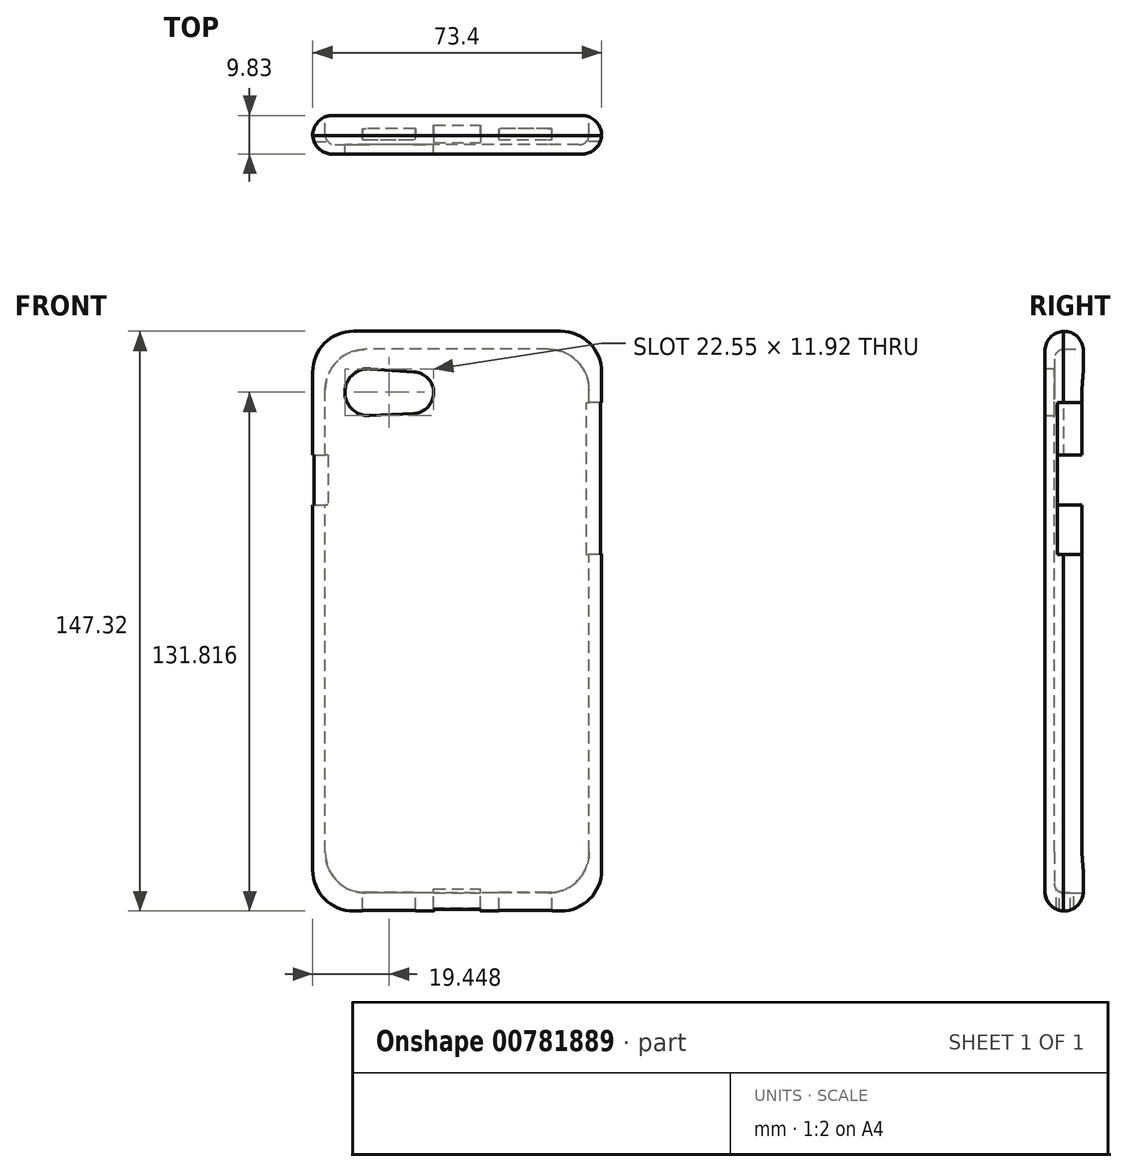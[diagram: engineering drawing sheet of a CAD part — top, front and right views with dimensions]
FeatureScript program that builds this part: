
annotation { "Feature Type Name" : "Feature", "Feature Type Description" : "" }
export const myFeature = defineFeature(function(context is Context, id is Id, definition is map)
    precondition{}
    {
        {
            var Q0;
            Q0=qCreatedBy(makeId("Front.planeOp"),FACE);
            var sketch = newSketch(context, id + "F0", { "sketchPlane" : qUnion([Q0])});
            skLineSegment(sketch, "E0.bottom", {"start": v(36.7, -73.66) * mm, "end": v(-36.7, -73.66) * mm});
            skLineSegment(sketch, "E0.top", {"start": v(36.7, 73.66) * mm, "end": v(-36.7, 73.66) * mm});
            skLineSegment(sketch, "E0.left", {"start": v(36.7, -73.66) * mm, "end": v(36.7, 73.66) * mm});
            skLineSegment(sketch, "E0.right", {"start": v(-36.7, -73.66) * mm, "end": v(-36.7, 73.66) * mm});
            skPoint(sketch, "E0.middle", {"position": v(0, 0) * mm});
            skCircle(sketch, "E1", {"center": v(-22.56, 58.16) * mm, "radius": 5.97 * mm});
            skLineSegment(sketch, "E2", {"start": v(-26.85, 73.66) * mm, "end": v(-26.85, 71.54) * mm});
            skLineSegment(sketch, "E3", {"start": v(-36.7, 59.19) * mm, "end": v(-34.57, 59.19) * mm});
            skLineSegment(sketch, "E4", {"start": v(-36.7, 73.66) * mm, "end": v(-28.82, 65.04) * mm});
            skCircle(sketch, "E5", {"center": v(-11.28, 58.05) * mm, "radius": 5.3 * mm});
            skLineSegment(sketch, "E6", {"start": v(-11.03, 52.74) * mm, "end": v(-22.27, 52.2) * mm});
            skLineSegment(sketch, "E7", {"start": v(-10.92, 63.34) * mm, "end": v(-22.15, 64.11) * mm});
            skLineSegment(sketch, "E8", {"start": v(-28.82, 65.04) * mm, "end": v(-22.15, 57.75) * mm});
            skLineSegment(sketch, "E9", {"start": v(-34.72, 71.5) * mm, "end": v(-36.7, 73.66) * mm});
            skLineSegment(sketch, "E10", {"start": v(-36.7, 73.66) * mm, "end": v(-33.75, 70.43) * mm});
            skSolve(sketch);
        }
        {
            var Q0;
            Q0 = qSketchRegion(id + "F0", true);
            extrude(context, id + "F1", {"entities" : qUnion([Q0]), "depth" : 9.83 * mm, "offsetDistance" : 25.4 * mm});
        }
        {
            var Q0;
            Q0=makeQuery(id+"F1.opExtrude","SWEPT_EDGE",EDGE,{"disambiguationData":[OSD([sQuery(id+"F0.wireOp",EDGE,"E0.bottom"),sQuery(id+"F0.wireOp",EDGE,"E0.left")])]});
            var Q1;
            Q1=makeQuery(id+"F1.opExtrude","SWEPT_EDGE",EDGE,{"disambiguationData":[OSD([sQuery(id+"F0.wireOp",EDGE,"E0.top"),sQuery(id+"F0.wireOp",EDGE,"E0.left")])]});
            var Q2;
            Q2=makeQuery(id+"F1.opExtrude","SWEPT_EDGE",EDGE,{"disambiguationData":[OSD([sQuery(id+"F0.wireOp",EDGE,"E0.bottom"),sQuery(id+"F0.wireOp",EDGE,"E0.right")])]});
            var Q3;
            Q3=makeQuery(id+"F1.opExtrude","SWEPT_EDGE",EDGE,{"disambiguationData":[OSD([sQuery(id+"F0.wireOp",EDGE,"E0.top"),sQuery(id+"F0.wireOp",EDGE,"E0.right")])]});
            fillet(context, id + "F2", {"entities" : qUnion([Q0, Q1, Q2, Q3]), "radius" : 10.4 * mm, "tangentPropagation" : true, "allowEdgeOverflow" : false});
        }
        {
            var Q0;
            Q0=qCreatedBy(makeId("Front.planeOp"),FACE);
            var sketch = newSketch(context, id + "F3", { "sketchPlane" : qUnion([Q0])});
            skLineSegment(sketch, "E11.bottom", {"start": v(33.53, -69.09) * mm, "end": v(-33.53, -69.09) * mm});
            skLineSegment(sketch, "E11.top", {"start": v(33.53, 69.09) * mm, "end": v(-33.53, 69.09) * mm});
            skLineSegment(sketch, "E11.left", {"start": v(33.53, -69.09) * mm, "end": v(33.53, 69.09) * mm});
            skLineSegment(sketch, "E11.right", {"start": v(-33.53, -69.09) * mm, "end": v(-33.53, 69.09) * mm});
            skPoint(sketch, "E11.middle", {"position": v(0, 0) * mm});
            skLineSegment(sketch, "E12", {"start": v(-33.53, -30.02) * mm, "end": v(-37.19, -30.02) * mm});
            skLineSegment(sketch, "E13", {"start": v(-6.36, 69.09) * mm, "end": v(-6.36, 72.75) * mm});
            skSolve(sketch);
        }
        {
            var Q0;
            {var subQ5=sQuery(id+"F3.wireOp",EDGE,"E11.bottom");Q0=makeQuery(id+"F3.imprint","IMPRINT",FACE,{"disambiguationData":[TD([[makeQuery(id+"F3.imprint","IMPRINT",EDGE,{"derivedFrom":subQ5}),-1.0]])]});}
            extrude(context, id + "F4", {"entities" : qUnion([Q0]), "operationType" : NewBodyOperationType.REMOVE, "depth" : 7.44 * mm, "offsetDistance" : 25.4 * mm});
        }
        {
            var Q0;
            Q0=qCreatedBy(makeId("Front.planeOp"),FACE);
            var sketch = newSketch(context, id + "F5", { "sketchPlane" : qUnion([Q0])});
            skLineSegment(sketch, "E14.bottom", {"start": v(31.5, -66.88) * mm, "end": v(-31.5, -66.88) * mm});
            skLineSegment(sketch, "E14.top", {"start": v(31.5, 66.88) * mm, "end": v(-31.5, 66.88) * mm});
            skLineSegment(sketch, "E14.left", {"start": v(31.5, -66.88) * mm, "end": v(31.5, 66.88) * mm});
            skLineSegment(sketch, "E14.right", {"start": v(-31.5, -66.88) * mm, "end": v(-31.5, 66.88) * mm});
            skPoint(sketch, "E14.middle", {"position": v(0, 0) * mm});
            skLineSegment(sketch, "E15", {"start": v(31.5, 66.88) * mm, "end": v(29.58, 65) * mm});
            skCircle(sketch, "E16", {"center": v(23.33, 58.66) * mm, "radius": 5.97 * mm});
            skLineSegment(sketch, "E17", {"start": v(23.37, 66.8) * mm, "end": v(23.37, 64.66) * mm});
            skLineSegment(sketch, "E18", {"start": v(31.4, 58.55) * mm, "end": v(29.26, 58.55) * mm});
            skLineSegment(sketch, "E19", {"start": v(29.58, 65) * mm, "end": v(27.59, 63.07) * mm});
            skLineSegment(sketch, "E20", {"start": v(29.26, 58.66) * mm, "end": v(6.77, 58.66) * mm});
            skCircle(sketch, "E21", {"center": v(12.08, 58.66) * mm, "radius": 5.28 * mm});
            skLineSegment(sketch, "E22", {"start": v(11.76, 63.92) * mm, "end": v(22.96, 64.62) * mm});
            skLineSegment(sketch, "E23", {"start": v(22.96, 52.7) * mm, "end": v(11.76, 53.4) * mm});
            skSolve(sketch);
        }
        {
            var Q0;
            Q0=makeQuery(id+"F4.boolean.opBoolean","COPY",EDGE,{"derivedFrom":makeQuery(id+"F4.opExtrude","SWEPT_EDGE",EDGE,{"disambiguationData":[OSD([sQuery(id+"F3.wireOp",EDGE,"E11.top"),sQuery(id+"F3.wireOp",EDGE,"E11.right")])]})});
            var Q1;
            Q1=makeQuery(id+"F4.boolean.opBoolean","COPY",EDGE,{"derivedFrom":makeQuery(id+"F4.opExtrude","SWEPT_EDGE",EDGE,{"disambiguationData":[OSD([sQuery(id+"F3.wireOp",EDGE,"E11.top"),sQuery(id+"F3.wireOp",EDGE,"E11.left")])]})});
            var Q2;
            Q2=makeQuery(id+"F4.boolean.opBoolean","COPY",EDGE,{"derivedFrom":makeQuery(id+"F4.opExtrude","SWEPT_EDGE",EDGE,{"disambiguationData":[OSD([sQuery(id+"F3.wireOp",EDGE,"E11.bottom"),sQuery(id+"F3.wireOp",EDGE,"E11.left")])]})});
            var Q3;
            Q3=makeQuery(id+"F4.boolean.opBoolean","COPY",EDGE,{"derivedFrom":makeQuery(id+"F4.opExtrude","SWEPT_EDGE",EDGE,{"disambiguationData":[OSD([sQuery(id+"F3.wireOp",EDGE,"E11.bottom"),sQuery(id+"F3.wireOp",EDGE,"E11.right")])]})});
            fillet(context, id + "F6", {"entities" : qUnion([Q0, Q1, Q2, Q3]), "radius" : 10.4 * mm, "tangentPropagation" : true, "allowEdgeOverflow" : false});
        }
        {
            var Q0;
            {var subQ0=sQuery(id+"F5.wireOp",EDGE,"E16");var subQ2=makeQuery(id+"F5.imprint","IMPRINT",VERTEX,{"derivedFrom":subQ0});Q0=makeQuery(id+"F5.imprint","IMPRINT",FACE,{"disambiguationData":[TD([[makeQuery(id+"F5.imprint","IMPRINT",EDGE,{"disambiguationData":[TD([[subQ2,1.0]])],"derivedFrom":subQ0}),1.0]])]});}
            var Q1;
            {var subQ0=sQuery(id+"F5.wireOp",EDGE,"E21");var subQ1=sQuery(id+"F5.wireOp",EDGE,"E16");var subQ2=makeQuery(id+"F5.imprint","INTERSECT",VERTEX,{"disambiguationData":[OD(0.0)],"derivedFrom":[subQ1,subQ0]});Q1=makeQuery(id+"F5.imprint","IMPRINT",FACE,{"disambiguationData":[TD([[makeQuery(id+"F5.imprint","IMPRINT",EDGE,{"disambiguationData":[TD([[subQ2,-1.0]])],"derivedFrom":subQ1}),-1.0]])]});}
            var Q2;
            {var subQ0=sQuery(id+"F5.wireOp",EDGE,"E20");var subQ1=sQuery(id+"F5.wireOp",EDGE,"E16");var subQ2=makeQuery(id+"F5.imprint","INTERSECT",VERTEX,{"derivedFrom":[subQ1,subQ0]});Q2=makeQuery(id+"F5.imprint","IMPRINT",FACE,{"disambiguationData":[TD([[makeQuery(id+"F5.imprint","IMPRINT",EDGE,{"disambiguationData":[TD([[subQ2,-1.0]])],"derivedFrom":subQ1}),-1.0]])]});}
            var Q3;
            {var subQ0=sQuery(id+"F5.wireOp",EDGE,"E23");Q3=makeQuery(id+"F5.imprint","IMPRINT",FACE,{"disambiguationData":[TD([[makeQuery(id+"F5.imprint","IMPRINT",EDGE,{"derivedFrom":subQ0}),-1.0]])]});}
            var Q4;
            {var subQ0=sQuery(id+"F5.wireOp",EDGE,"E22");Q4=makeQuery(id+"F5.imprint","IMPRINT",FACE,{"disambiguationData":[TD([[makeQuery(id+"F5.imprint","IMPRINT",EDGE,{"derivedFrom":subQ0}),-1.0]])]});}
            extrude(context, id + "F7", {"entities" : qUnion([Q0, Q1, Q2, Q3, Q4]), "operationType" : NewBodyOperationType.REMOVE, "oppositeDirection" : true, "depth" : 25.4 * mm, "offsetDistance" : 25.4 * mm});
        }
        {
            var Q0;
            Q0=makeQuery(id+"F1.opExtrude","CAP_EDGE",EDGE,{"disambiguationData":[OSD([sQuery(id+"F0.wireOp",EDGE,"E0.right")])],"isStart":true});
            fillet(context, id + "F8", {"entities" : qUnion([Q0]), "radius" : 5.08 * mm, "tangentPropagation" : true, "allowEdgeOverflow" : false});
        }
        {
            var Q0;
            Q0=makeQuery(id+"F1.opExtrude","CAP_EDGE",EDGE,{"disambiguationData":[OSD([sQuery(id+"F0.wireOp",EDGE,"E0.right")])],"isStart":false});
            fillet(context, id + "F9", {"entities" : qUnion([Q0]), "radius" : 5.08 * mm, "tangentPropagation" : true, "allowEdgeOverflow" : false});
        }
        {
            var Q0;
            Q0=qCreatedBy(makeId("Top.planeOp"),FACE);
            var sketch = newSketch(context, id + "F10", { "sketchPlane" : qUnion([Q0])});
            skLineSegment(sketch, "E24.bottom", {"start": v(5.97, -2.5) * mm, "end": v(-5.97, -2.5) * mm});
            skLineSegment(sketch, "E24.top", {"start": v(5.97, -6.94) * mm, "end": v(-5.97, -6.94) * mm});
            skLineSegment(sketch, "E24.left", {"start": v(5.97, -2.5) * mm, "end": v(5.97, -6.94) * mm});
            skLineSegment(sketch, "E24.right", {"start": v(-5.97, -2.5) * mm, "end": v(-5.97, -6.94) * mm});
            skPoint(sketch, "E24.middle", {"position": v(0, -4.72) * mm});
            skLineSegment(sketch, "E25", {"start": v(5.97, -5.08) * mm, "end": v(10.57, -5.08) * mm});
            skLineSegment(sketch, "E26", {"start": v(-10.57, -5.08) * mm, "end": v(-5.97, -5.08) * mm});
            skLineSegment(sketch, "E27.bottom", {"start": v(-24.06, -6.13) * mm, "end": v(-10.58, -6.13) * mm});
            skLineSegment(sketch, "E27.top", {"start": v(-24.06, -3.31) * mm, "end": v(-10.58, -3.31) * mm});
            skLineSegment(sketch, "E27.left", {"start": v(-24.06, -6.13) * mm, "end": v(-24.06, -3.31) * mm});
            skLineSegment(sketch, "E27.right", {"start": v(-10.58, -6.13) * mm, "end": v(-10.58, -3.31) * mm});
            skPoint(sketch, "E27.middle", {"position": v(-17.32, -4.72) * mm});
            skLineSegment(sketch, "E28.bottom", {"start": v(10.57, -6.13) * mm, "end": v(24.06, -6.13) * mm});
            skLineSegment(sketch, "E28.top", {"start": v(10.57, -3.3) * mm, "end": v(24.06, -3.3) * mm});
            skLineSegment(sketch, "E28.left", {"start": v(10.57, -6.13) * mm, "end": v(10.57, -3.3) * mm});
            skLineSegment(sketch, "E28.right", {"start": v(24.06, -6.13) * mm, "end": v(24.06, -3.3) * mm});
            skPoint(sketch, "E28.middle", {"position": v(17.32, -4.72) * mm});
            skSolve(sketch);
        }
        {
            var Q0;
            Q0 = qSketchRegion(id + "F10", true);
            extrude(context, id + "F11", {"entities" : qUnion([Q0]), "operationType" : NewBodyOperationType.REMOVE, "oppositeDirection" : true, "depth" : 76.2 * mm, "offsetDistance" : 25.4 * mm});
        }
        {
            var Q0;
            Q0=qCreatedBy(makeId("Right.planeOp"),FACE);
            var sketch = newSketch(context, id + "F12", { "sketchPlane" : qUnion([Q0])});
            skLineSegment(sketch, "E29.bottom", {"start": v(-6.63, 16.95) * mm, "end": v(0.03, 16.95) * mm});
            skLineSegment(sketch, "E29.top", {"start": v(-6.63, 55.56) * mm, "end": v(0.03, 55.56) * mm});
            skLineSegment(sketch, "E29.left", {"start": v(-6.63, 16.95) * mm, "end": v(-6.63, 55.56) * mm});
            skLineSegment(sketch, "E29.right", {"start": v(0.03, 16.95) * mm, "end": v(0.03, 55.56) * mm});
            skPoint(sketch, "E29.middle", {"position": v(-3.3, 36.26) * mm});
            skSolve(sketch);
        }
        {
            var Q0;
            Q0 = qSketchRegion(id + "F12", true);
            extrude(context, id + "F13", {"entities" : qUnion([Q0]), "operationType" : NewBodyOperationType.REMOVE, "endBound" : BoundingType.THROUGH_ALL, "depth" : 63.5 * mm, "offsetDistance" : 25.4 * mm});
        }
        {
            var Q0;
            Q0=qCreatedBy(makeId("Right.planeOp"),FACE);
            var sketch = newSketch(context, id + "F14", { "sketchPlane" : qUnion([Q0])});
            skLineSegment(sketch, "E30.bottom", {"start": v(-6.65, 42.16) * mm, "end": v(0, 42.16) * mm});
            skLineSegment(sketch, "E30.top", {"start": v(-6.65, 29.53) * mm, "end": v(0, 29.53) * mm});
            skLineSegment(sketch, "E30.left", {"start": v(-6.65, 42.16) * mm, "end": v(-6.65, 29.53) * mm});
            skLineSegment(sketch, "E30.right", {"start": v(0, 42.16) * mm, "end": v(0, 29.53) * mm});
            skPoint(sketch, "E30.middle", {"position": v(-3.32, 35.84) * mm});
            skSolve(sketch);
        }
        {
            var Q0;
            Q0 = qSketchRegion(id + "F14", true);
            extrude(context, id + "F15", {"entities" : qUnion([Q0]), "operationType" : NewBodyOperationType.REMOVE, "endBound" : BoundingType.THROUGH_ALL, "oppositeDirection" : true, "depth" : 63.5 * mm, "offsetDistance" : 25.4 * mm});
        }
        {
            var Q0;
            Q0=makeQuery(id+"F4.boolean.opBoolean","COPY",EDGE,{"derivedFrom":makeQuery(id+"F4.opExtrude","CAP_EDGE",EDGE,{"disambiguationData":[OSD([sQuery(id+"F3.wireOp",EDGE,"E11.right")])],"isStart":false})});
            fillet(context, id + "F16", {"entities" : qUnion([Q0]), "radius" : 2.54 * mm, "tangentPropagation" : true, "allowEdgeOverflow" : false});
        }
    });
